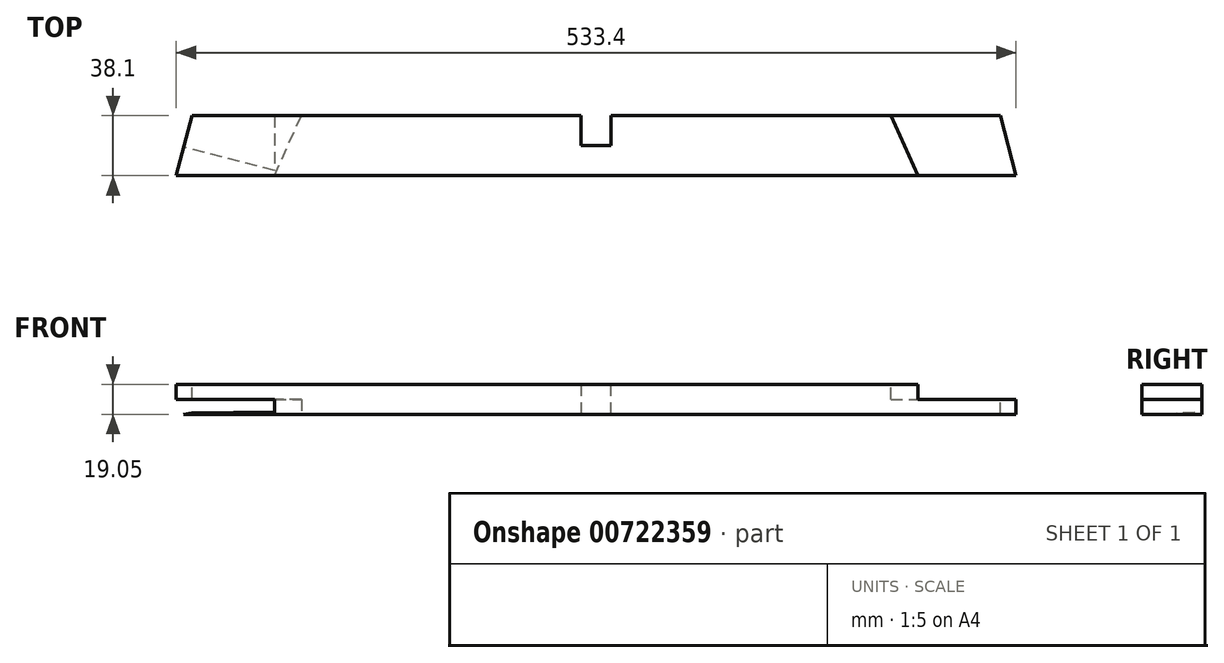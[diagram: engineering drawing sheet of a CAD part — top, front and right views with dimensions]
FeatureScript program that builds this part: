
annotation { "Feature Type Name" : "Feature", "Feature Type Description" : "" }
export const myFeature = defineFeature(function(context is Context, id is Id, definition is map)
    precondition{}
    {
        {
            var Q0;
            Q0=qCreatedBy(makeId("Front.planeOp"),FACE);
            var sketch = newSketch(context, id + "F0", { "sketchPlane" : qUnion([Q0])});
            skLineSegment(sketch, "E0.bottom", {"start": v(0, 0) * mm, "end": v(-533.4, 0) * mm});
            skLineSegment(sketch, "E0.top", {"start": v(0, 19.05) * mm, "end": v(-533.4, 19.05) * mm});
            skLineSegment(sketch, "E0.left", {"start": v(0, 0) * mm, "end": v(0, 19.05) * mm});
            skLineSegment(sketch, "E0.right", {"start": v(-533.4, 0) * mm, "end": v(-533.4, 19.05) * mm});
            skSolve(sketch);
        }
        {
            var Q0;
            Q0=qSketchRegion(id+"F0",true);
            extrude(context, id + "F1", {"entities" : qUnion([Q0]), "depth" : 38.1 * mm, "offsetDistance" : 25.4 * mm});
        }
        {
            var Q0;
            Q0=makeQuery(id+"F1.opExtrude","SWEPT_FACE",FACE,{"disambiguationData":[OSD([sQuery(id+"F0.wireOp",EDGE,"E0.top")])]});
            var sketch = newSketch(context, id + "F2", { "sketchPlane" : qUnion([Q0])});
            skLineSegment(sketch, "E1", {"start": v(-533.4, -38.1) * mm, "end": v(-523.42, 0) * mm});
            skLineSegment(sketch, "E2", {"start": v(-523.42, 0) * mm, "end": v(-533.4, 0) * mm});
            skLineSegment(sketch, "E3", {"start": v(-533.4, 0) * mm, "end": v(-533.4, -38.1) * mm});
            skSolve(sketch);
        }
        {
            var Q0;
            Q0=qSketchRegion(id+"F2",true);
            extrude(context, id + "F3", {"entities" : qUnion([Q0]), "operationType" : NewBodyOperationType.REMOVE, "oppositeDirection" : true, "depth" : 50.8 * mm, "offsetDistance" : 25.4 * mm});
        }
        {
            var Q0;
            Q0=makeQuery(id+"F1.opExtrude","SWEPT_FACE",FACE,{"disambiguationData":[OSD([sQuery(id+"F0.wireOp",EDGE,"E0.top")])]});
            var sketch = newSketch(context, id + "F4", { "sketchPlane" : qUnion([Q0])});
            skLineSegment(sketch, "E4", {"start": v(0, -38.1) * mm, "end": v(-9.98, 0) * mm});
            skLineSegment(sketch, "E5", {"start": v(-9.98, 0) * mm, "end": v(0, 0) * mm});
            skLineSegment(sketch, "E6", {"start": v(0, 0) * mm, "end": v(0, -38.1) * mm});
            skSolve(sketch);
        }
        {
            var Q0;
            Q0=qSketchRegion(id+"F4",true);
            extrude(context, id + "F5", {"entities" : qUnion([Q0]), "operationType" : NewBodyOperationType.REMOVE, "oppositeDirection" : true, "depth" : 76.2 * mm, "offsetDistance" : 25.4 * mm});
        }
        {
            var Q0;
            Q0=makeQuery(id+"F3.boolean.opBoolean","COPY",FACE,{"derivedFrom":makeQuery(id+"F3.opExtrude","SWEPT_FACE",FACE,{"disambiguationData":[OSD([sQuery(id+"F2.wireOp",EDGE,"E1")])]})});
            var sketch = newSketch(context, id + "F6", { "sketchPlane" : qUnion([Q0])});
            skLineSegment(sketch, "E7", {"start": v(153.17, 0) * mm, "end": v(171.99, 0) * mm});
            skLineSegment(sketch, "E8", {"start": v(171.99, 9.53) * mm, "end": v(171.99, 0) * mm});
            skLineSegment(sketch, "E9", {"start": v(171.99, 0) * mm, "end": v(171.99, 9.53) * mm, "construction": true});
            skLineSegment(sketch, "E10", {"start": v(171.99, 9.53) * mm, "end": v(-58.74, 9.52) * mm});
            skLineSegment(sketch, "E11", {"start": v(153.17, 0) * mm, "end": v(-58.74, 9.52) * mm});
            skSolve(sketch);
        }
        {
            var Q0;
            Q0=qSketchRegion(id+"F6",true);
            extrude(context, id + "F7", {"entities" : qUnion([Q0]), "operationType" : NewBodyOperationType.REMOVE, "oppositeDirection" : true, "depth" : 60.32 * mm, "offsetDistance" : 25.4 * mm});
        }
        {
            var Q0;
            Q0=makeQuery(id+"F1.opExtrude","SWEPT_FACE",FACE,{"disambiguationData":[OSD([sQuery(id+"F0.wireOp",EDGE,"E0.bottom")])]});
            var sketch = newSketch(context, id + "F8", { "sketchPlane" : qUnion([Q0])});
            skLineSegment(sketch, "E12", {"start": v(-471.04, 0) * mm, "end": v(-471.04, 38.1) * mm});
            skLineSegment(sketch, "E13", {"start": v(-471.04, 0) * mm, "end": v(-453.87, 0) * mm});
            skLineSegment(sketch, "E14", {"start": v(-471.04, 38.1) * mm, "end": v(-453.87, 0) * mm});
            skSolve(sketch);
        }
        {
            var Q0;
            Q0=qSketchRegion(id+"F8",true);
            extrude(context, id + "F9", {"entities" : qUnion([Q0]), "operationType" : NewBodyOperationType.REMOVE, "oppositeDirection" : true, "depth" : 9.52 * mm, "offsetDistance" : 25.4 * mm});
        }
        {
            var Q0;
            Q0=makeQuery(id+"F5.boolean.opBoolean","COPY",FACE,{"derivedFrom":makeQuery(id+"F5.opExtrude","SWEPT_FACE",FACE,{"disambiguationData":[OSD([sQuery(id+"F4.wireOp",EDGE,"E4")])]})});
            var sketch = newSketch(context, id + "F10", { "sketchPlane" : qUnion([Q0])});
            skLineSegment(sketch, "E15", {"start": v(-36.86, 19.05) * mm, "end": v(-36.86, 0) * mm, "construction": true});
            skLineSegment(sketch, "E16", {"start": v(-36.86, 9.52) * mm, "end": v(45.27, 9.52) * mm});
            skLineSegment(sketch, "E17", {"start": v(-36.86, 19.05) * mm, "end": v(-36.86, 9.52) * mm});
            skLineSegment(sketch, "E18", {"start": v(-36.86, 19.05) * mm, "end": v(45.63, 19.05) * mm});
            skLineSegment(sketch, "E19", {"start": v(45.63, 19.05) * mm, "end": v(45.27, 9.52) * mm});
            skSolve(sketch);
        }
        {
            var Q0;
            Q0=qSketchRegion(id+"F10",true);
            extrude(context, id + "F11", {"entities" : qUnion([Q0]), "operationType" : NewBodyOperationType.REMOVE, "oppositeDirection" : true, "depth" : 60.32 * mm, "offsetDistance" : 25.4 * mm});
        }
        {
            var Q0;
            Q0=makeQuery(id+"F1.opExtrude","CAP_FACE",FACE,{"disambiguationData":[OSD([sQuery(id+"F0.wireOp",EDGE,"E0.bottom"),sQuery(id+"F0.wireOp",EDGE,"E0.top"),sQuery(id+"F0.wireOp",EDGE,"E0.left"),sQuery(id+"F0.wireOp",EDGE,"E0.right")])],"isStart":true});
            var sketch = newSketch(context, id + "F12", { "sketchPlane" : qUnion([Q0])});
            skLineSegment(sketch, "E20", {"start": v(276.23, 19.05) * mm, "end": v(276.23, 0) * mm});
            skLineSegment(sketch, "E21", {"start": v(257.18, 0) * mm, "end": v(257.18, 19.05) * mm});
            skLineSegment(sketch, "E22", {"start": v(276.23, 19.05) * mm, "end": v(257.18, 19.05) * mm});
            skLineSegment(sketch, "E23", {"start": v(257.18, 0) * mm, "end": v(276.23, 0) * mm});
            skPoint(sketch, "E24.endSnap0", {"position": v(297.88, 19.05) * mm});
            skLineSegment(sketch, "E25", {"start": v(523.42, 9.52) * mm, "end": v(9.98, 9.52) * mm, "construction": true});
            skLineSegment(sketch, "E26", {"start": v(257.18, 9.52) * mm, "end": v(276.23, 9.52) * mm, "construction": true});
            skLineSegment(sketch, "E27", {"start": v(266.7, 9.52) * mm, "end": v(266.7, 0) * mm, "construction": true});
            skSolve(sketch);
        }
        {
            var Q0;
            Q0=qSketchRegion(id+"F12",true);
            extrude(context, id + "F13", {"entities" : qUnion([Q0]), "operationType" : NewBodyOperationType.REMOVE, "oppositeDirection" : true, "depth" : 19.05 * mm, "offsetDistance" : 25.4 * mm});
        }
        {
            var Q0;
            Q0=makeQuery(id+"F1.opExtrude","SWEPT_FACE",FACE,{"disambiguationData":[OSD([sQuery(id+"F0.wireOp",EDGE,"E0.top")])]});
            var sketch = newSketch(context, id + "F14", { "sketchPlane" : qUnion([Q0])});
            skLineSegment(sketch, "E28", {"start": v(-79.53, 0) * mm, "end": v(-62.36, -38.1) * mm});
            skLineSegment(sketch, "E29", {"start": v(-62.36, 0) * mm, "end": v(-79.53, 0) * mm});
            skLineSegment(sketch, "E30", {"start": v(-62.36, -38.1) * mm, "end": v(-62.36, 0) * mm});
            skSolve(sketch);
        }
        {
            var Q0;
            Q0=qSketchRegion(id+"F14",true);
            extrude(context, id + "F15", {"entities" : qUnion([Q0]), "operationType" : NewBodyOperationType.REMOVE, "oppositeDirection" : true, "depth" : 9.52 * mm, "offsetDistance" : 25.4 * mm});
        }
    });
